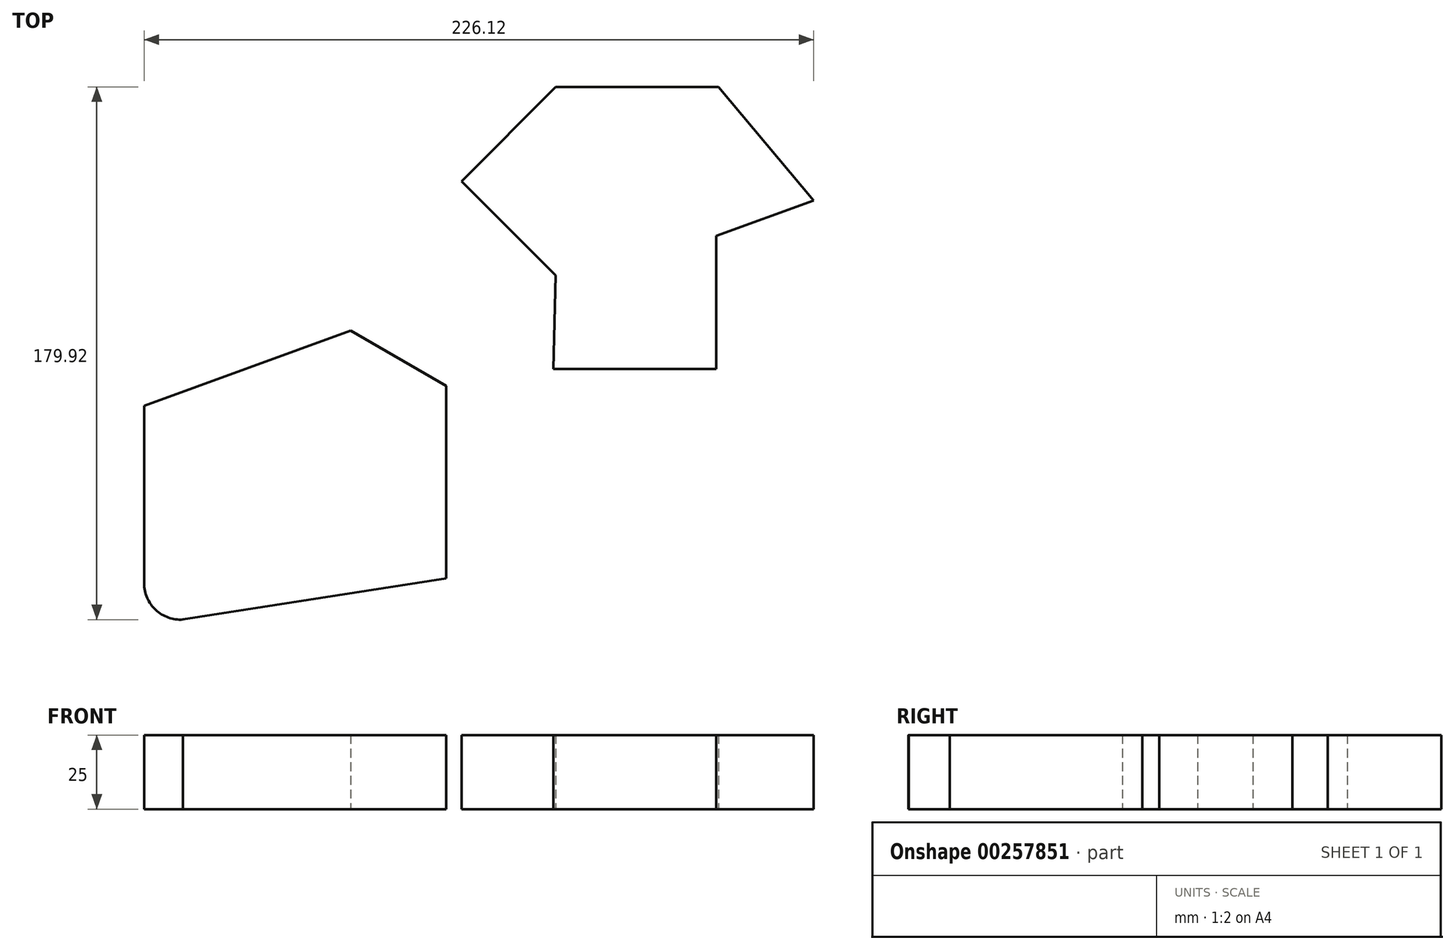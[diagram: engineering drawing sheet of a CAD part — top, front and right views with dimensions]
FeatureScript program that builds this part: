
annotation { "Feature Type Name" : "Feature", "Feature Type Description" : "" }
export const myFeature = defineFeature(function(context is Context, id is Id, definition is map)
    precondition{}
    {
        {
            var Q0;
            Q0=qCreatedBy(makeId("Top.planeOp"),FACE);
            var sketch = newSketch(context, id + "F0", { "sketchPlane" : qUnion([Q0])});
            skLineSegment(sketch, "E0", {"start": v(-5.14, 10.45) * mm, "end": v(-5.14, -54.55) * mm});
            skLineSegment(sketch, "E1", {"start": v(-5.14, 10.45) * mm, "end": v(-26.74, 10.45) * mm});
            skLineSegment(sketch, "E2", {"start": v(-5.14, 10.45) * mm, "end": v(-37.48, 29.12) * mm});
            skLineSegment(sketch, "E3", {"start": v(-37.48, 29.12) * mm, "end": v(-107.16, 3.75) * mm});
            skLineSegment(sketch, "E4", {"start": v(-107.16, 3.75) * mm, "end": v(-59.52, 3.75) * mm});
            skLineSegment(sketch, "E5", {"start": v(-107.16, 3.75) * mm, "end": v(-107.16, -56.25) * mm});
            skLineSegment(sketch, "E6", {"start": v(-5.14, -54.55) * mm, "end": v(-94.06, -68.47) * mm});
            skArc(sketch, "E7", {"start": v(-107.16, -56.25) * mm, "mid": v(-103.27, -65.2) * mm, "end": v(-94.06, -68.47) * mm});
            skLineSegment(sketch, "E8", {"start": v(31.82, 111.42) * mm, "end": v(86.82, 111.42) * mm});
            skLineSegment(sketch, "E9", {"start": v(31.82, 111.42) * mm, "end": v(0, 79.6) * mm});
            skLineSegment(sketch, "E10", {"start": v(86.82, 111.42) * mm, "end": v(118.96, 73.12) * mm});
            skLineSegment(sketch, "E11", {"start": v(118.96, 73.12) * mm, "end": v(86.07, 61.15) * mm});
            skLineSegment(sketch, "E12", {"start": v(118.96, 73.12) * mm, "end": v(73.06, 73.12) * mm});
            skLineSegment(sketch, "E13", {"start": v(86.07, 61.15) * mm, "end": v(86.07, 16.15) * mm});
            skLineSegment(sketch, "E14", {"start": v(86.07, 16.15) * mm, "end": v(31.07, 16.15) * mm});
            skLineSegment(sketch, "E15", {"start": v(0, 79.6) * mm, "end": v(32, 79.6) * mm});
            skLineSegment(sketch, "E16", {"start": v(0, 79.6) * mm, "end": v(31.82, 47.78) * mm});
            skLineSegment(sketch, "E17", {"start": v(31.82, 47.78) * mm, "end": v(31.07, 16.15) * mm});
            skSolve(sketch);
        }
        {
            var Q0;
            Q0 = qSketchRegion(id + "F0", true);
            extrude(context, id + "F1", {"entities" : qUnion([Q0]), "depth" : 25 * mm});
        }
    });
